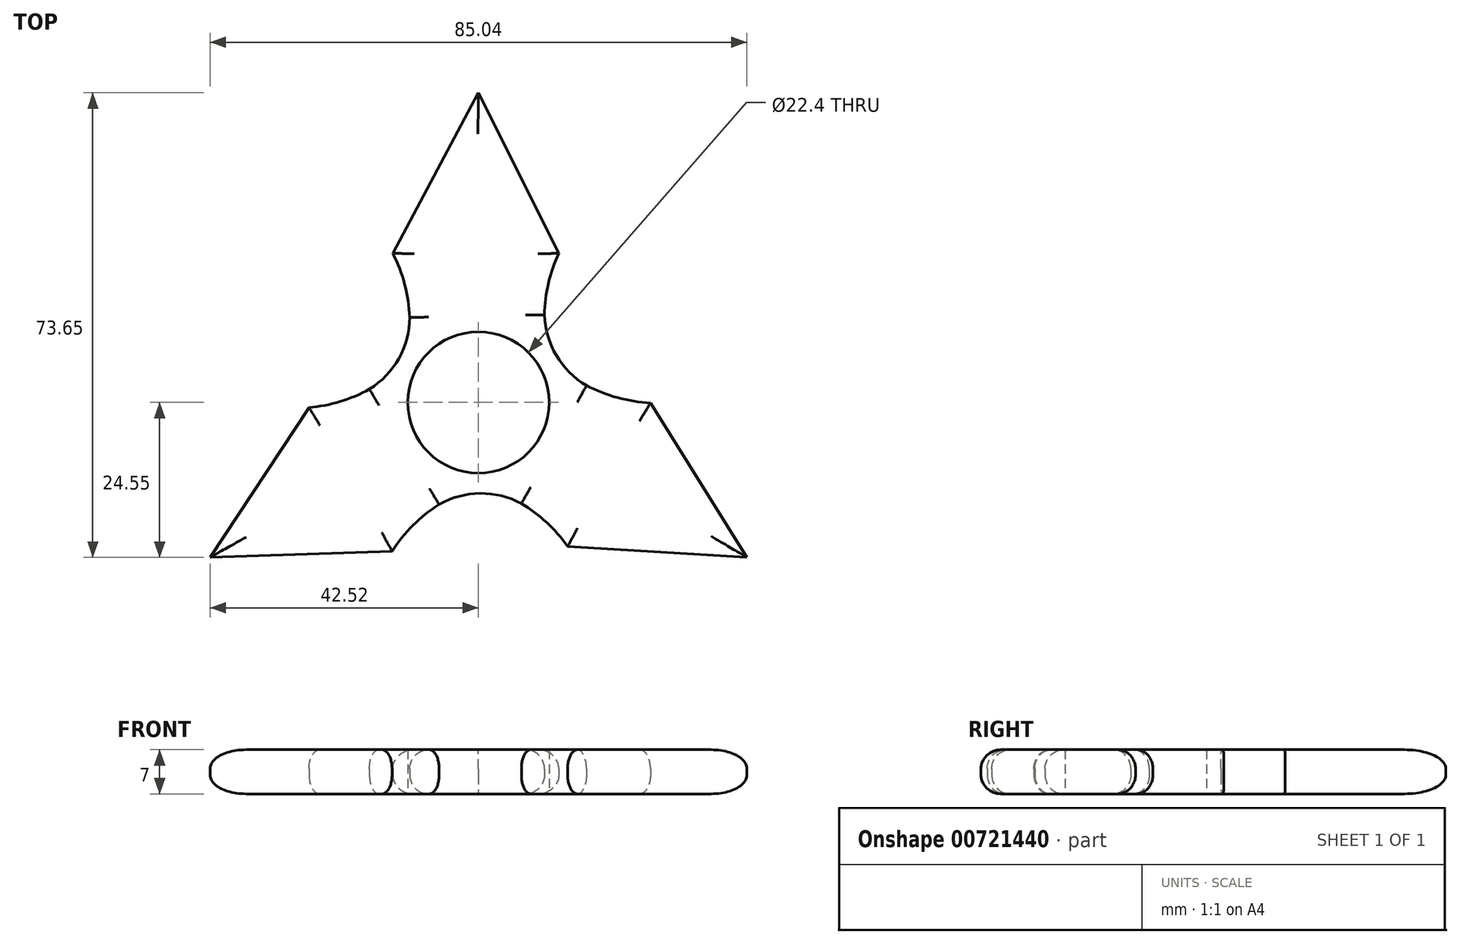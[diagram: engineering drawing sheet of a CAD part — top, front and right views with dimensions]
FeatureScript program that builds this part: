
annotation { "Feature Type Name" : "Feature", "Feature Type Description" : "" }
export const myFeature = defineFeature(function(context is Context, id is Id, definition is map)
    precondition{}
    {
        {
            var Q0;
            Q0=qCreatedBy(makeId("Top.planeOp"),FACE);
            var sketch = newSketch(context, id + "F0", { "sketchPlane" : qUnion([Q0])});
            skCircle(sketch, "E0", {"center": v(0, 0) * mm, "radius": 11.2 * mm});
            skPoint(sketch, "E1.start.orphan", {"position": v(0, 37.63) * mm});
            skLineSegment(sketch, "E2", {"start": v(0, 49.1) * mm, "end": v(-13.57, 23.64) * mm});
            skLineSegment(sketch, "E3", {"start": v(0, 49.1) * mm, "end": v(12.73, 23.64) * mm});
            skArc(sketch, "E4", {"start": v(-13, 2.25) * mm, "mid": v(-10.87, 13) * mm, "end": v(-13.57, 23.64) * mm});
            skArc(sketch, "E5", {"start": v(12.73, 23.64) * mm, "mid": v(10.46, 13.57) * mm, "end": v(12.73, 3.5) * mm});
            skLineSegment(sketch, "E6.1.0", {"start": v(-42.52, -24.55) * mm, "end": v(-26.84, -0.8) * mm});
            skLineSegment(sketch, "E6.1.1", {"start": v(-42.52, -24.55) * mm, "end": v(-13.69, -23.57) * mm});
            skArc(sketch, "E6.1.2", {"start": v(4.55, -12.4) * mm, "mid": v(-5.83, -15.92) * mm, "end": v(-13.69, -23.57) * mm});
            skArc(sketch, "E6.1.3", {"start": v(-26.84, -0.8) * mm, "mid": v(-16.98, 2.28) * mm, "end": v(-9.4, 9.28) * mm});
            skLineSegment(sketch, "E6.2.0", {"start": v(42.52, -24.55) * mm, "end": v(14.1, -22.84) * mm});
            skLineSegment(sketch, "E6.2.1", {"start": v(42.52, -24.55) * mm, "end": v(27.26, -0.07) * mm});
            skArc(sketch, "E6.2.2", {"start": v(8.45, 10.14) * mm, "mid": v(16.7, 2.9) * mm, "end": v(27.26, -0.07) * mm});
            skArc(sketch, "E6.2.3", {"start": v(14.1, -22.84) * mm, "mid": v(6.52, -15.85) * mm, "end": v(-3.34, -12.77) * mm});
            skArc(sketch, "E7", {"start": v(-19.9, 0.85) * mm, "mid": v(-13.4, 5.74) * mm, "end": v(-10.88, 13.48) * mm});
            skArc(sketch, "E8.1.0", {"start": v(9.21, -17.66) * mm, "mid": v(1.72, -14.48) * mm, "end": v(-6.23, -16.17) * mm});
            skArc(sketch, "E8.2.0", {"start": v(10.69, 16.8) * mm, "mid": v(11.67, 8.73) * mm, "end": v(17.12, 2.69) * mm});
            skSolve(sketch);
        }
        {
            var Q0;
            Q0=qSketchRegion(id+"F0",true);
            extrude(context, id + "F1", {"entities" : qUnion([Q0]), "depth" : 7 * mm, "offsetDistance" : 25 * mm});
        }
        {
            var Q0;
            Q0=makeQuery(id+"F1.opExtrude","CAP_EDGE",EDGE,{"disambiguationData":[OSD([sQuery(id+"F0.wireOp",EDGE,"E2")])],"isStart":false});
            var Q1;
            Q1=makeQuery(id+"F1.opExtrude","CAP_EDGE",EDGE,{"disambiguationData":[OSD([sQuery(id+"F0.wireOp",EDGE,"E4")])],"isStart":false});
            var Q2;
            Q2=makeQuery(id+"F1.opExtrude","CAP_EDGE",EDGE,{"disambiguationData":[OSD([sQuery(id+"F0.wireOp",EDGE,"E7")])],"isStart":false});
            var Q3;
            Q3=makeQuery(id+"F1.opExtrude","CAP_EDGE",EDGE,{"disambiguationData":[OSD([sQuery(id+"F0.wireOp",EDGE,"E6.1.3")])],"isStart":false});
            var Q4;
            Q4=makeQuery(id+"F1.opExtrude","CAP_EDGE",EDGE,{"disambiguationData":[OSD([sQuery(id+"F0.wireOp",EDGE,"E6.1.0")])],"isStart":false});
            var Q5;
            Q5=makeQuery(id+"F1.opExtrude","CAP_EDGE",EDGE,{"disambiguationData":[OSD([sQuery(id+"F0.wireOp",EDGE,"E6.1.1")])],"isStart":false});
            var Q6;
            Q6=makeQuery(id+"F1.opExtrude","CAP_EDGE",EDGE,{"disambiguationData":[OSD([sQuery(id+"F0.wireOp",EDGE,"E6.1.2")])],"isStart":false});
            var Q7;
            Q7=makeQuery(id+"F1.opExtrude","CAP_EDGE",EDGE,{"disambiguationData":[OSD([sQuery(id+"F0.wireOp",EDGE,"E8.1.0")])],"isStart":false});
            var Q8;
            Q8=makeQuery(id+"F1.opExtrude","CAP_EDGE",EDGE,{"disambiguationData":[OSD([sQuery(id+"F0.wireOp",EDGE,"E6.2.3")])],"isStart":false});
            var Q9;
            Q9=makeQuery(id+"F1.opExtrude","CAP_EDGE",EDGE,{"disambiguationData":[OSD([sQuery(id+"F0.wireOp",EDGE,"E6.2.0")])],"isStart":false});
            var Q10;
            Q10=makeQuery(id+"F1.opExtrude","CAP_EDGE",EDGE,{"disambiguationData":[OSD([sQuery(id+"F0.wireOp",EDGE,"E6.2.1")])],"isStart":false});
            var Q11;
            Q11=makeQuery(id+"F1.opExtrude","CAP_EDGE",EDGE,{"disambiguationData":[OSD([sQuery(id+"F0.wireOp",EDGE,"E6.2.2")])],"isStart":false});
            var Q12;
            Q12=makeQuery(id+"F1.opExtrude","CAP_EDGE",EDGE,{"disambiguationData":[OSD([sQuery(id+"F0.wireOp",EDGE,"E8.2.0")])],"isStart":false});
            var Q13;
            Q13=makeQuery(id+"F1.opExtrude","CAP_EDGE",EDGE,{"disambiguationData":[OSD([sQuery(id+"F0.wireOp",EDGE,"E5")])],"isStart":false});
            var Q14;
            Q14=makeQuery(id+"F1.opExtrude","CAP_EDGE",EDGE,{"disambiguationData":[OSD([sQuery(id+"F0.wireOp",EDGE,"E3")])],"isStart":false});
            var Q15;
            Q15=makeQuery(id+"F1.opExtrude","CAP_EDGE",EDGE,{"disambiguationData":[OSD([sQuery(id+"F0.wireOp",EDGE,"E3")])],"isStart":true});
            var Q16;
            Q16=makeQuery(id+"F1.opExtrude","CAP_EDGE",EDGE,{"disambiguationData":[OSD([sQuery(id+"F0.wireOp",EDGE,"E5")])],"isStart":true});
            var Q17;
            Q17=makeQuery(id+"F1.opExtrude","CAP_EDGE",EDGE,{"disambiguationData":[OSD([sQuery(id+"F0.wireOp",EDGE,"E8.2.0")])],"isStart":true});
            var Q18;
            Q18=makeQuery(id+"F1.opExtrude","CAP_EDGE",EDGE,{"disambiguationData":[OSD([sQuery(id+"F0.wireOp",EDGE,"E6.2.2")])],"isStart":true});
            var Q19;
            Q19=makeQuery(id+"F1.opExtrude","CAP_EDGE",EDGE,{"disambiguationData":[OSD([sQuery(id+"F0.wireOp",EDGE,"E6.2.1")])],"isStart":true});
            var Q20;
            Q20=makeQuery(id+"F1.opExtrude","CAP_EDGE",EDGE,{"disambiguationData":[OSD([sQuery(id+"F0.wireOp",EDGE,"E6.2.0")])],"isStart":true});
            var Q21;
            Q21=makeQuery(id+"F1.opExtrude","CAP_EDGE",EDGE,{"disambiguationData":[OSD([sQuery(id+"F0.wireOp",EDGE,"E6.2.3")])],"isStart":true});
            var Q22;
            Q22=makeQuery(id+"F1.opExtrude","CAP_EDGE",EDGE,{"disambiguationData":[OSD([sQuery(id+"F0.wireOp",EDGE,"E8.1.0")])],"isStart":true});
            var Q23;
            Q23=makeQuery(id+"F1.opExtrude","CAP_EDGE",EDGE,{"disambiguationData":[OSD([sQuery(id+"F0.wireOp",EDGE,"E6.1.2")])],"isStart":true});
            var Q24;
            Q24=makeQuery(id+"F1.opExtrude","CAP_EDGE",EDGE,{"disambiguationData":[OSD([sQuery(id+"F0.wireOp",EDGE,"E6.1.1")])],"isStart":true});
            var Q25;
            Q25=makeQuery(id+"F1.opExtrude","CAP_EDGE",EDGE,{"disambiguationData":[OSD([sQuery(id+"F0.wireOp",EDGE,"E6.1.0")])],"isStart":true});
            var Q26;
            Q26=makeQuery(id+"F1.opExtrude","CAP_EDGE",EDGE,{"disambiguationData":[OSD([sQuery(id+"F0.wireOp",EDGE,"E6.1.3")])],"isStart":true});
            var Q27;
            Q27=makeQuery(id+"F1.opExtrude","CAP_EDGE",EDGE,{"disambiguationData":[OSD([sQuery(id+"F0.wireOp",EDGE,"E7")])],"isStart":true});
            var Q28;
            Q28=makeQuery(id+"F1.opExtrude","CAP_EDGE",EDGE,{"disambiguationData":[OSD([sQuery(id+"F0.wireOp",EDGE,"E4")])],"isStart":true});
            var Q29;
            Q29=makeQuery(id+"F1.opExtrude","CAP_EDGE",EDGE,{"disambiguationData":[OSD([sQuery(id+"F0.wireOp",EDGE,"E2")])],"isStart":true});
            fillet(context, id + "F2", {"entities" : qUnion([Q0, Q1, Q2, Q3, Q4, Q5, Q6, Q7, Q8, Q9, Q10, Q11, Q12, Q13, Q14, Q15, Q16, Q17, Q18, Q19, Q20, Q21, Q22, Q23, Q24, Q25, Q26, Q27, Q28, Q29]), "radius" : 3 * mm, "tangentPropagation" : true, "allowEdgeOverflow" : false});
        }
    });
